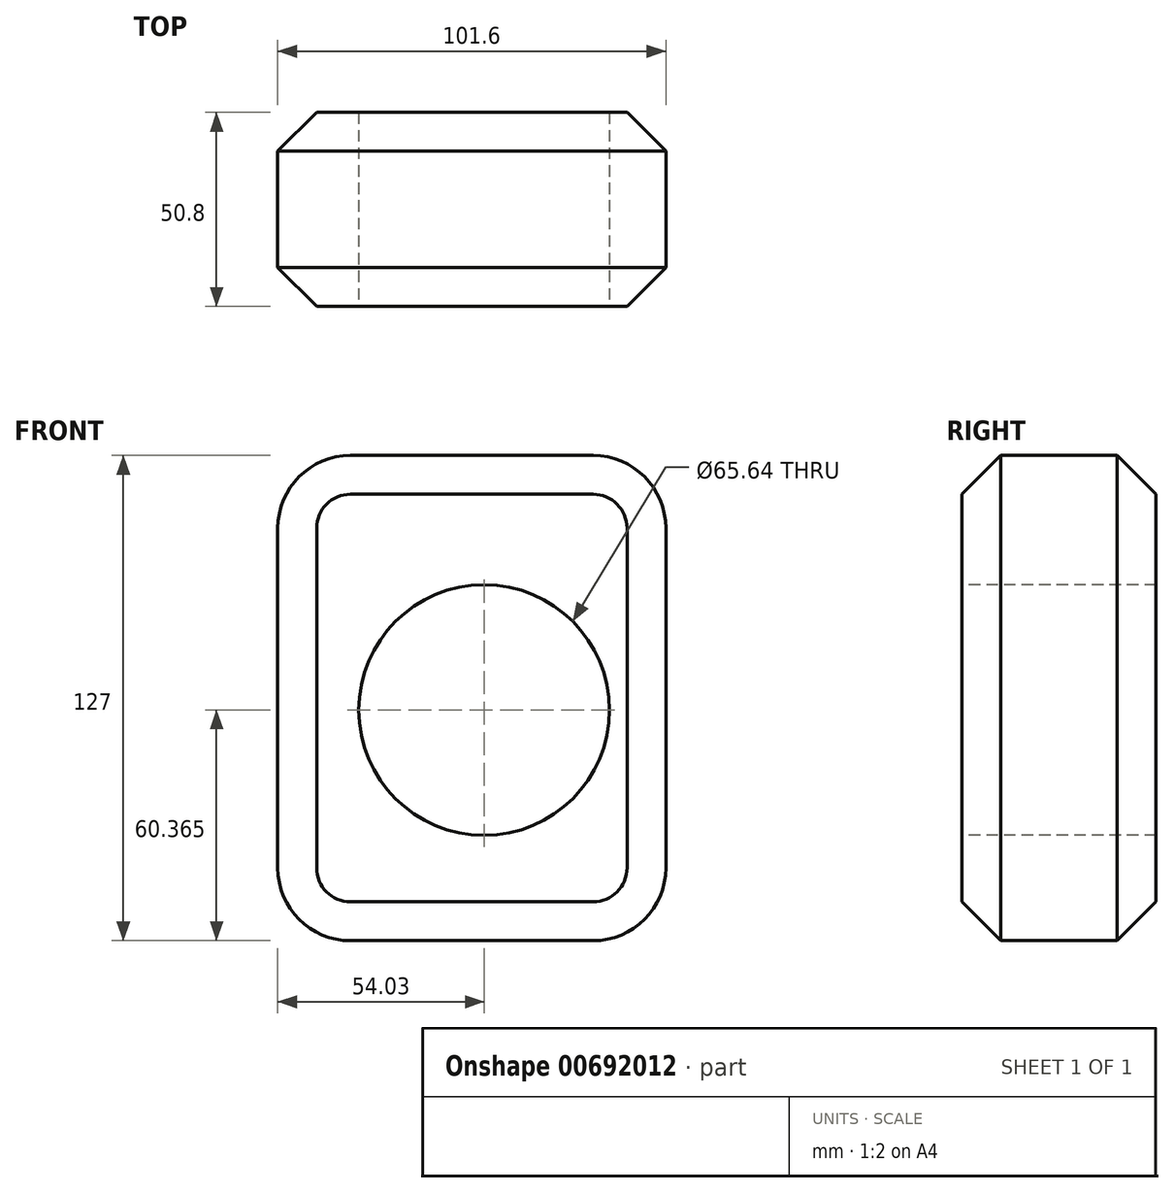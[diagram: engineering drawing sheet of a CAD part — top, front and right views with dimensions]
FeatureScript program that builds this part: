
annotation { "Feature Type Name" : "Feature", "Feature Type Description" : "" }
export const myFeature = defineFeature(function(context is Context, id is Id, definition is map)
    precondition{}
    {
        {
            var Q0;
            Q0=qCreatedBy(makeId("Top.planeOp"),FACE);
            var sketch = newSketch(context, id + "F0", { "sketchPlane" : qUnion([Q0])});
            skLineSegment(sketch, "E0.bottom", {"start": v(0, 50.8) * mm, "end": v(101.6, 50.8) * mm});
            skLineSegment(sketch, "E0.top", {"start": v(0, 0) * mm, "end": v(101.6, 0) * mm});
            skLineSegment(sketch, "E0.left", {"start": v(0, 50.8) * mm, "end": v(0, 0) * mm});
            skLineSegment(sketch, "E0.right", {"start": v(101.6, 50.8) * mm, "end": v(101.6, 0) * mm});
            skSolve(sketch);
        }
        {
            var Q0;
            Q0=makeQuery(id+"F0.imprint","IMPRINT",FACE,{"disambiguationData":[TD([[makeQuery(id+"F0.imprint","IMPRINT",EDGE,{"derivedFrom":sQuery(id+"F0.wireOp",EDGE,"E0.bottom")}),-1.0]])]});
            extrude(context, id + "F1", {"entities" : qUnion([Q0]), "depth" : 127 * mm, "offsetDistance" : 25.4 * mm});
        }
        {
            var Q0;
            Q0=makeQuery(id+"F1.opExtrude","SWEPT_FACE",FACE,{"disambiguationData":[OSD([sQuery(id+"F0.wireOp",EDGE,"E0.top")])]});
            var sketch = newSketch(context, id + "F2", { "sketchPlane" : qUnion([Q0])});
            skCircle(sketch, "E1", {"center": v(54.03, 60.37) * mm, "radius": 32.82 * mm});
            skSolve(sketch);
        }
        {
            var Q0;
            Q0=makeQuery(id+"F2.imprint","IMPRINT",FACE,{"disambiguationData":[TD([[makeQuery(id+"F2.imprint","IMPRINT",EDGE,{"derivedFrom":sQuery(id+"F2.wireOp",EDGE,"E1")}),1.0]])]});
            extrude(context, id + "F3", {"entities" : qUnion([Q0]), "operationType" : NewBodyOperationType.REMOVE, "oppositeDirection" : true, "depth" : 120.24 * mm, "offsetDistance" : 25.4 * mm});
        }
        {
            var Q0;
            Q0=makeQuery(id+"F1.opExtrude","CAP_EDGE",EDGE,{"disambiguationData":[OSD([sQuery(id+"F0.wireOp",EDGE,"E0.right")])],"isStart":false});
            var Q1;
            Q1=makeQuery(id+"F1.opExtrude","CAP_EDGE",EDGE,{"disambiguationData":[OSD([sQuery(id+"F0.wireOp",EDGE,"E0.left")])],"isStart":false});
            var Q2;
            Q2=makeQuery(id+"F1.opExtrude","CAP_EDGE",EDGE,{"disambiguationData":[OSD([sQuery(id+"F0.wireOp",EDGE,"E0.right")])],"isStart":true});
            var Q3;
            Q3=makeQuery(id+"F1.opExtrude","CAP_EDGE",EDGE,{"disambiguationData":[OSD([sQuery(id+"F0.wireOp",EDGE,"E0.left")])],"isStart":true});
            fillet(context, id + "F4", {"entities" : qUnion([Q0, Q1, Q2, Q3]), "radius" : 19.05 * mm, "tangentPropagation" : true, "allowEdgeOverflow" : false});
        }
        {
            var Q0;
            Q0=makeQuery(id+"F1.opExtrude","SWEPT_EDGE",EDGE,{"disambiguationData":[OSD([sQuery(id+"F0.wireOp",EDGE,"E0.top"),sQuery(id+"F0.wireOp",EDGE,"E0.right")])]});
            var Q1;
            Q1=makeQuery(id+"F1.opExtrude","SWEPT_EDGE",EDGE,{"disambiguationData":[OSD([sQuery(id+"F0.wireOp",EDGE,"E0.bottom"),sQuery(id+"F0.wireOp",EDGE,"E0.left")])]});
            chamfer(context, id + "F5", {"entities" : qUnion([Q0, Q1]), "chamferType" : ChamferType.OFFSET_ANGLE, "width" : 10.16 * mm, "oppositeDirection" : false, "angle" : 45 * degree, "tangentPropagation" : true});
        }
    });
